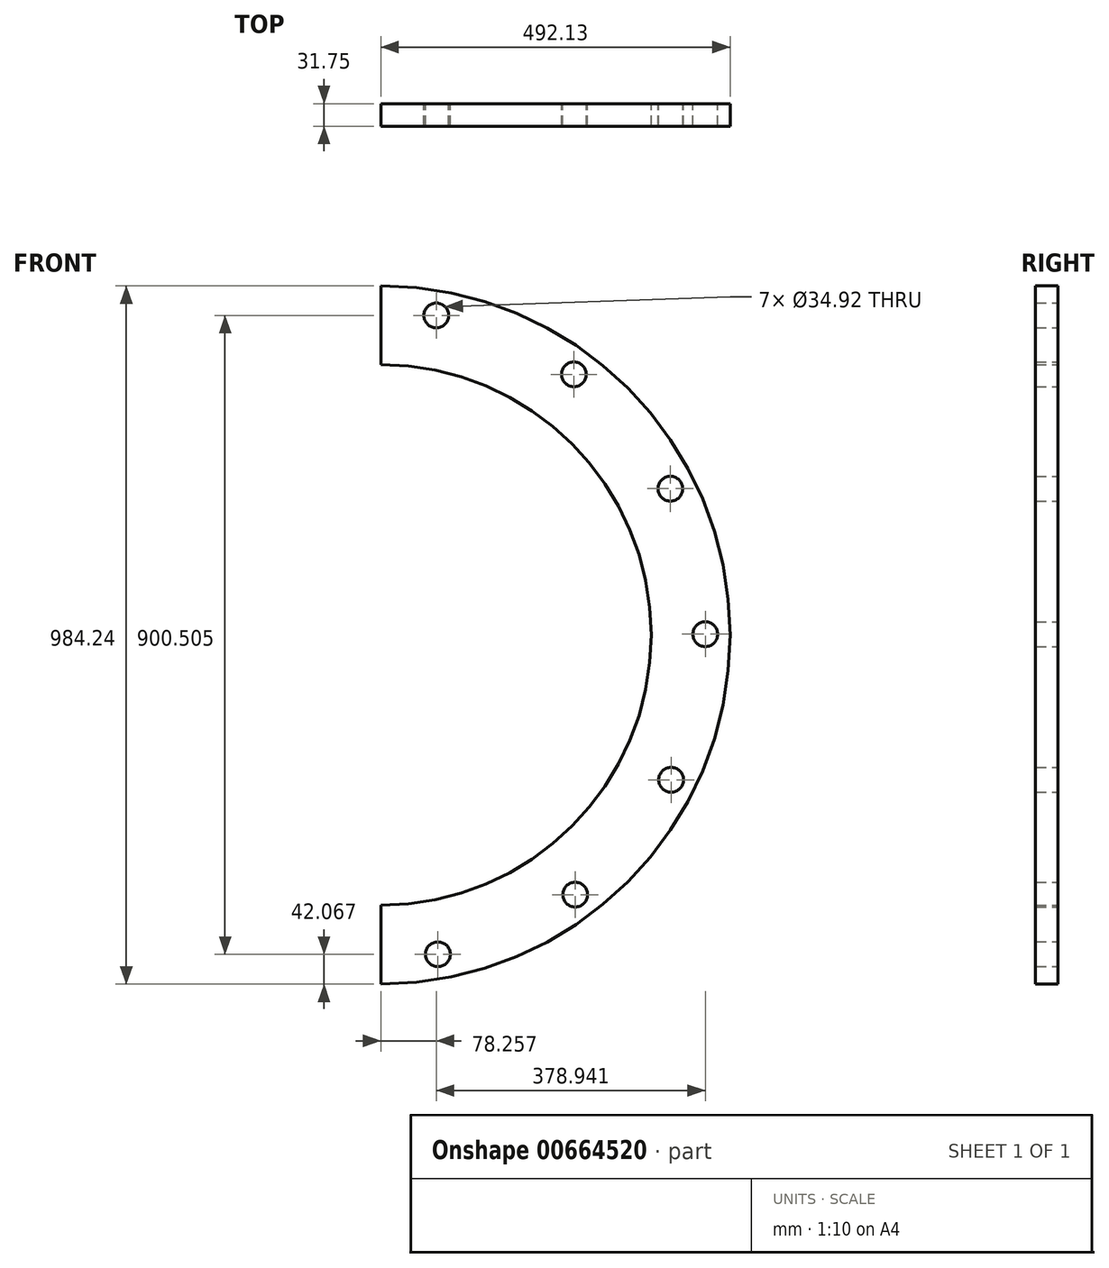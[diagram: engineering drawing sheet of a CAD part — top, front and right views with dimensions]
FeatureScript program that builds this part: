
annotation { "Feature Type Name" : "Feature", "Feature Type Description" : "" }
export const myFeature = defineFeature(function(context is Context, id is Id, definition is map)
    precondition{}
    {
        {
            var Q0;
            Q0=qCreatedBy(makeId("Front.planeOp"),FACE);
            var sketch = newSketch(context, id + "F0", { "sketchPlane" : qUnion([Q0])});
            skArc(sketch, "E0", {"start": v(0, 492.13) * mm, "mid": v(492.13, 0) * mm, "end": v(0, -492.13) * mm});
            skArc(sketch, "E1", {"start": v(0, 381) * mm, "mid": v(381, 0) * mm, "end": v(0, -381) * mm});
            skLineSegment(sketch, "E2", {"start": v(0, -381) * mm, "end": v(0, -492.13) * mm});
            skLineSegment(sketch, "E3", {"start": v(0, 381) * mm, "end": v(0, 492.13) * mm});
            skCircle(sketch, "E4.converted", {"center": v(0, 0) * mm, "radius": 457.2 * mm, "construction": true});
            skPoint(sketch, "E5.orphan", {"position": v(0, 457.2) * mm});
            skCircle(sketch, "E6", {"center": v(78.26, 450.45) * mm, "radius": 17.46 * mm});
            skCircle(sketch, "E7.1.0", {"center": v(272.1, 367.42) * mm, "radius": 17.46 * mm});
            skCircle(sketch, "E7.2.0", {"center": v(408.05, 206.22) * mm, "radius": 17.46 * mm});
            skCircle(sketch, "E7.3.0", {"center": v(457.2, 1.15) * mm, "radius": 17.46 * mm});
            skCircle(sketch, "E7.4.0", {"center": v(409.08, -204.16) * mm, "radius": 17.46 * mm});
            skCircle(sketch, "E7.5.0", {"center": v(273.94, -366.04) * mm, "radius": 17.46 * mm});
            skLineSegment(sketch, "E7.anchor1", {"start": v(0, 0) * mm, "end": v(78.26, 450.45) * mm, "construction": true});
            skLineSegment(sketch, "E7.anchor2", {"start": v(0, 0) * mm, "end": v(80.53, -450.05) * mm, "construction": true});
            skCircle(sketch, "E8.1.6.0", {"center": v(80.53, -450.05) * mm, "radius": 17.46 * mm});
            skSolve(sketch);
        }
        {
            var Q0;
            Q0 = qSketchRegion(id + "F0", true);
            extrude(context, id + "F1", {"entities" : qUnion([Q0]), "depth" : 25.4 * mm, "offsetDistance" : 25.4 * mm});
        }
        {
            var Q0;
            Q0=makeQuery(id+"F1.opExtrude","CAP_FACE",FACE,{"disambiguationData":[OSD([sQuery(id+"F0.wireOp",EDGE,"E0"),sQuery(id+"F0.wireOp",EDGE,"E1"),sQuery(id+"F0.wireOp",EDGE,"E2"),sQuery(id+"F0.wireOp",EDGE,"E3")])],"isStart":false});
            extrude(context, id + "F2", {"entities" : qUnion([Q0]), "operationType" : NewBodyOperationType.ADD, "depth" : 6.35 * mm, "offsetDistance" : 25.4 * mm});
        }
    });
